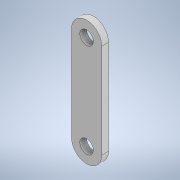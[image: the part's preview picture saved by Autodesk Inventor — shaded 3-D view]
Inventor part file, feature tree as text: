
AUTODESK INVENTOR PART (.ipt)
format: ipt  version: 2021 (Build 250183000, 183)  size: 131,584 bytes
history: native  units: mm
features: extrude x3, sketch x3, plane x1, fillet x1
ambient origin geometry x8: Origin, YZ Plane, XZ Plane, XY Plane, X Axis, Y Axis, Z Axis, Center Point
bodies: Solid1 (feature_tree)
feature tree (8):
  plane  "Work Plane1"
  extrude  "Extrusion2"  Depth=65.0mm
  fillet  "Fillet1"  Radius=9.0mm
  extrude  "Extrusion3"  Depth=4.0mm TaperAngle=0.0deg
  extrude  "Extrusion4"  Depth=18.0mm
  sketch  "Sketch2"  dims[d4=3.5mm d5=65.0mm]
  sketch  "Sketch3"  dims[d6=2.0mm d7=2.0mm d8=0.0mm d9=0.0mm d10=9.0mm]
  sketch  "Sketch4"  dims[d11=8.0mm d13=2.0mm d14=0.0mm d15=18.0mm d17=0.0mm d18=8.0mm d19=18.0mm d20=4.0mm d21=0.0mm]
